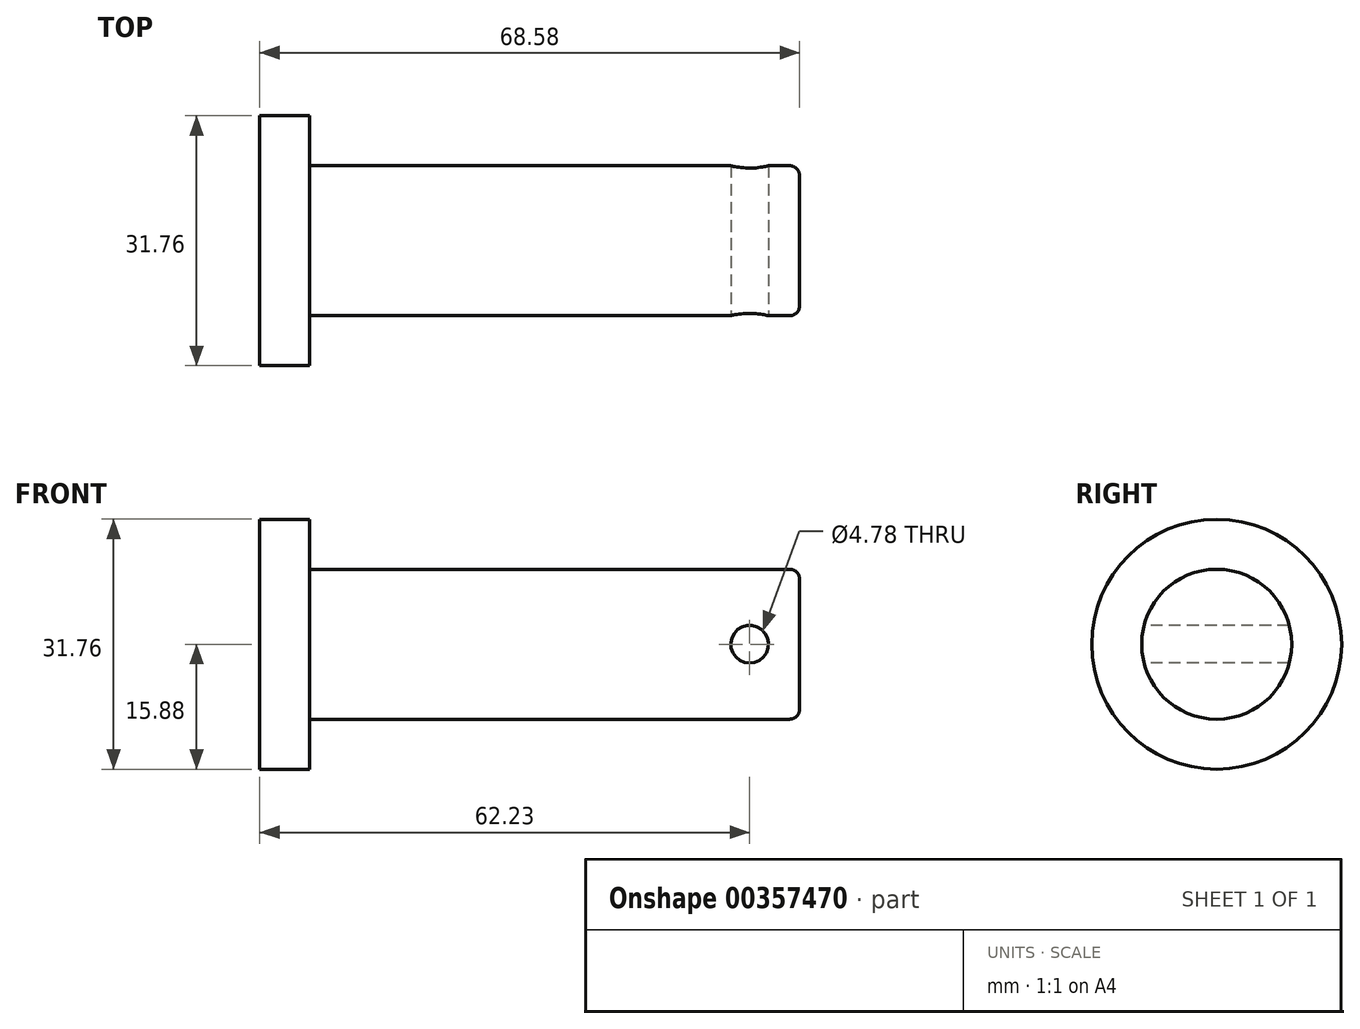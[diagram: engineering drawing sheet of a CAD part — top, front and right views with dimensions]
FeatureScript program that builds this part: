
annotation { "Feature Type Name" : "Feature", "Feature Type Description" : "" }
export const myFeature = defineFeature(function(context is Context, id is Id, definition is map)
    precondition{}
    {
        {
            var Q0;
            Q0=qCreatedBy(makeId("Right.planeOp"),FACE);
            var sketch = newSketch(context, id + "F0", { "sketchPlane" : qUnion([Q0])});
            skCircle(sketch, "E0", {"center": v(0, 0) * mm, "radius": 9.53 * mm});
            skSolve(sketch);
        }
        {
            var Q0;
            Q0=makeQuery(id+"F0.imprint","IMPRINT",FACE,{"disambiguationData":[TD([[makeQuery(id+"F0.imprint","IMPRINT",EDGE,{"derivedFrom":sQuery(id+"F0.wireOp",EDGE,"E0")}),1.0]])]});
            extrude(context, id + "F1", {"entities" : qUnion([Q0]), "depth" : 62.23 * mm});
        }
        {
            var Q0;
            Q0=qCreatedBy(makeId("Front.planeOp"),FACE);
            cPlane(context, id + "F2", {"entities" : qUnion([Q0]), "cplaneType" : CPlaneType.OFFSET, "offset" : 10.67 * mm, "width" : 152.4 * mm, "height" : 152.4 * mm});
        }
        {
            var Q0;
            Q0=qCreatedBy(id+"F2.planeOp",FACE);
            var sketch = newSketch(context, id + "F3", { "sketchPlane" : qUnion([Q0])});
            skCircle(sketch, "E1", {"center": v(55.88, 0) * mm, "radius": 2.39 * mm});
            skSolve(sketch);
        }
        {
            var Q0;
            Q0=makeQuery(id+"F3.imprint","IMPRINT",FACE,{"disambiguationData":[TD([[makeQuery(id+"F3.imprint","IMPRINT",EDGE,{"derivedFrom":sQuery(id+"F3.wireOp",EDGE,"E1")}),1.0]])]});
            extrude(context, id + "F4", {"entities" : qUnion([Q0]), "operationType" : NewBodyOperationType.REMOVE, "endBound" : BoundingType.THROUGH_ALL, "oppositeDirection" : true, "depth" : 25.4 * mm});
        }
        {
            var Q0;
            Q0=makeQuery(id+"F1.opExtrude","CAP_FACE",FACE,{"disambiguationData":[OSD([sQuery(id+"F0.wireOp",EDGE,"E0")])],"isStart":true});
            var sketch = newSketch(context, id + "F5", { "sketchPlane" : qUnion([Q0])});
            skCircle(sketch, "E2", {"center": v(0, 0) * mm, "radius": 15.88 * mm});
            skSolve(sketch);
        }
        {
            var Q0;
            Q0=makeQuery(id+"F5.imprint","IMPRINT",FACE,{"disambiguationData":[TD([[makeQuery(id+"F5.imprint","IMPRINT",EDGE,{"derivedFrom":sQuery(id+"F5.wireOp",EDGE,"E2")}),1.0]])]});
            var Q1;
            Q1=makeQuery(id+"F5.imprint","IMPRINT",FACE,{"disambiguationData":[TD([[makeQuery(id+"F5.imprint","IMPRINT",EDGE,{"derivedFrom":makeQuery(id+"F1.opExtrude","CAP_EDGE",EDGE,{"disambiguationData":[OSD([sQuery(id+"F0.wireOp",EDGE,"E0")])],"isStart":true})}),-1.0]])]});
            extrude(context, id + "F6", {"entities" : qUnion([Q0, Q1]), "operationType" : NewBodyOperationType.ADD, "depth" : 6.35 * mm});
        }
        {
            var Q0;
            Q0=makeQuery(id+"F1.opExtrude","CAP_EDGE",EDGE,{"disambiguationData":[OSD([sQuery(id+"F0.wireOp",EDGE,"E0")])],"isStart":false});
            fillet(context, id + "F7", {"entities" : qUnion([Q0]), "radius" : 1.27 * mm, "tangentPropagation" : true, "allowEdgeOverflow" : false});
        }
    });
